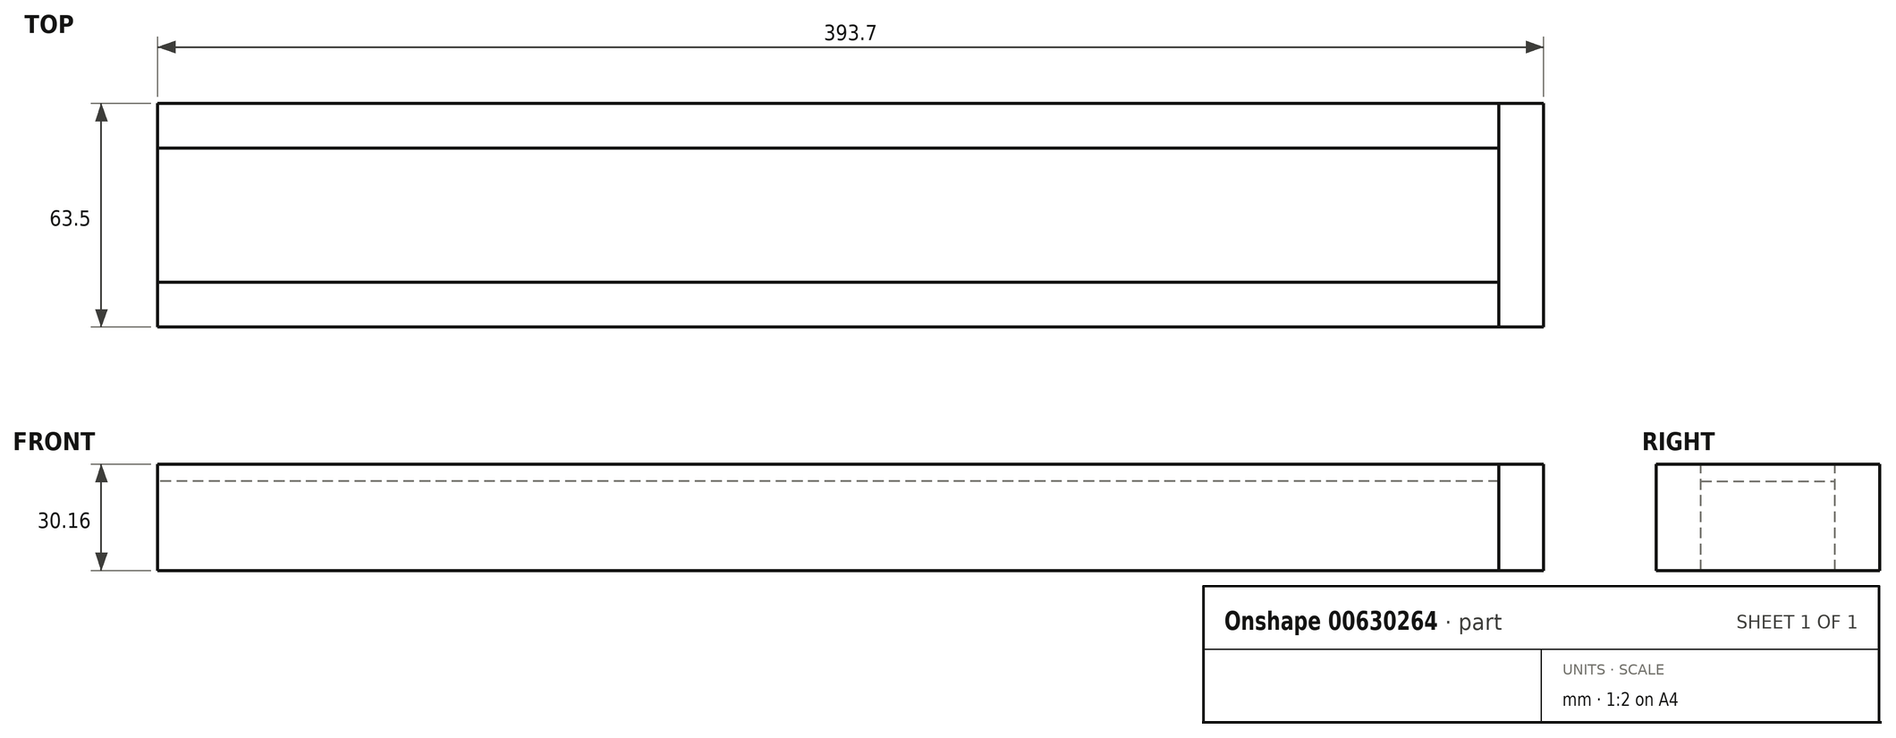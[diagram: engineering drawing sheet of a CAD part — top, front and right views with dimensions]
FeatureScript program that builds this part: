
annotation { "Feature Type Name" : "Feature", "Feature Type Description" : "" }
export const myFeature = defineFeature(function(context is Context, id is Id, definition is map)
    precondition{}
    {
        {
            var Q0;
            Q0=qCreatedBy(makeId("Right.planeOp"),FACE);
            var sketch = newSketch(context, id + "F0", { "sketchPlane" : qUnion([Q0])});
            skLineSegment(sketch, "E0.bottom", {"start": v(0, 0) * mm, "end": v(12.7, 0) * mm});
            skLineSegment(sketch, "E0.top", {"start": v(0, 30.16) * mm, "end": v(12.7, 30.16) * mm});
            skLineSegment(sketch, "E0.left", {"start": v(0, 0) * mm, "end": v(0, 30.16) * mm});
            skLineSegment(sketch, "E0.right", {"start": v(12.7, 0) * mm, "end": v(12.7, 30.16) * mm});
            skLineSegment(sketch, "E1.bottom", {"start": v(12.7, 0) * mm, "end": v(50.8, 0) * mm});
            skLineSegment(sketch, "E1.top", {"start": v(12.7, 25.4) * mm, "end": v(50.8, 25.4) * mm});
            skLineSegment(sketch, "E1.left", {"start": v(12.7, 0) * mm, "end": v(12.7, 25.4) * mm});
            skLineSegment(sketch, "E1.right", {"start": v(50.8, 0) * mm, "end": v(50.8, 25.4) * mm});
            skLineSegment(sketch, "E2.bottom", {"start": v(50.8, 0) * mm, "end": v(63.5, 0) * mm});
            skLineSegment(sketch, "E2.top", {"start": v(50.8, 30.16) * mm, "end": v(63.5, 30.16) * mm});
            skLineSegment(sketch, "E2.left", {"start": v(50.8, 0) * mm, "end": v(50.8, 30.16) * mm});
            skLineSegment(sketch, "E2.right", {"start": v(63.5, 0) * mm, "end": v(63.5, 30.16) * mm});
            skSolve(sketch);
        }
        {
            var Q0;
            Q0=makeQuery(id+"F0.imprint","IMPRINT",FACE,{"disambiguationData":[TD([[makeQuery(id+"F0.imprint","IMPRINT",EDGE,{"derivedFrom":sQuery(id+"F0.wireOp",EDGE,"E0.bottom")}),1.0]])]});
            var Q1;
            {var subQ3=sQuery(id+"F0.wireOp",EDGE,"E2.bottom");Q1=makeQuery(id+"F0.imprint","IMPRINT",FACE,{"disambiguationData":[TD([[makeQuery(id+"F0.imprint","IMPRINT",EDGE,{"derivedFrom":subQ3}),1.0]])]});}
            extrude(context, id + "F1", {"entities" : qUnion([Q0, Q1]), "depth" : 406.4 * mm, "offsetDistance" : 25.4 * mm});
        }
        {
            var Q0;
            {var subQ0=sQuery(id+"F0.wireOp",EDGE,"E1.bottom");Q0=makeQuery(id+"F0.imprint","IMPRINT",FACE,{"disambiguationData":[TD([[makeQuery(id+"F0.imprint","IMPRINT",EDGE,{"derivedFrom":subQ0}),1.0]])]});}
            var Q1;
            Q1=makeQuery(id+"F1.opExtrude","CAP_FACE",FACE,{"disambiguationData":[OSD([sQuery(id+"F0.wireOp",EDGE,"E0.bottom"),sQuery(id+"F0.wireOp",EDGE,"E0.top"),sQuery(id+"F0.wireOp",EDGE,"E0.left"),sQuery(id+"F0.wireOp",EDGE,"E0.right"),sQuery(id+"F0.wireOp",EDGE,"E1.left")])],"isStart":false});
            extrude(context, id + "F2", {"entities" : qUnion([Q0]), "endBound" : BoundingType.UP_TO_SURFACE, "depth" : 25.4 * mm, "endBoundEntityFace" : qUnion([Q1]), "offsetDistance" : 25.4 * mm});
        }
        {
            var Q0;
            Q0=makeQuery(id+"F1.opExtrude","SWEPT_FACE",FACE,{"disambiguationData":[OSD([sQuery(id+"F0.wireOp",EDGE,"E2.top")])]});
            var sketch = newSketch(context, id + "F3", { "sketchPlane" : qUnion([Q0])});
            skLineSegment(sketch, "E3", {"start": v(406.4, 63.5) * mm, "end": v(406.4, 0) * mm});
            skLineSegment(sketch, "E4", {"start": v(406.4, 0) * mm, "end": v(381, 0) * mm});
            skLineSegment(sketch, "E5", {"start": v(381, 0) * mm, "end": v(381, 63.5) * mm});
            skLineSegment(sketch, "E6", {"start": v(381, 63.5) * mm, "end": v(406.4, 63.5) * mm});
            skSolve(sketch);
        }
        {
            var Q0;
            Q0 = qSketchRegion(id + "F3", true);
            extrude(context, id + "F4", {"entities" : qUnion([Q0]), "operationType" : NewBodyOperationType.REMOVE, "endBound" : BoundingType.THROUGH_ALL, "oppositeDirection" : true, "depth" : 25.4 * mm, "offsetDistance" : 25.4 * mm});
        }
        {
            var Q0;
            Q0=qCreatedBy(makeId("Top.planeOp"),FACE);
            var sketch = newSketch(context, id + "F5", { "sketchPlane" : qUnion([Q0])});
            skLineSegment(sketch, "E7", {"start": v(381, 63.5) * mm, "end": v(393.7, 63.5) * mm});
            skLineSegment(sketch, "E8", {"start": v(393.7, 63.5) * mm, "end": v(393.7, 0) * mm});
            skLineSegment(sketch, "E9", {"start": v(393.7, 0) * mm, "end": v(381, 0) * mm});
            skLineSegment(sketch, "E10", {"start": v(381, 0) * mm, "end": v(381, 63.5) * mm});
            skSolve(sketch);
        }
        {
            var Q0;
            Q0 = qSketchRegion(id + "F5", true);
            var Q1;
            Q1=makeQuery(id+"F1.opExtrude","SWEPT_FACE",FACE,{"disambiguationData":[OSD([sQuery(id+"F0.wireOp",EDGE,"E2.top")])]});
            extrude(context, id + "F6", {"entities" : qUnion([Q0]), "endBound" : BoundingType.UP_TO_SURFACE, "depth" : 25.4 * mm, "endBoundEntityFace" : qUnion([Q1]), "offsetDistance" : 25.4 * mm});
        }
    });
